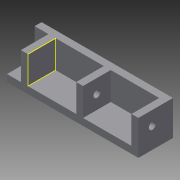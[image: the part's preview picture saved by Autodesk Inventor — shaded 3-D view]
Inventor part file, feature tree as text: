
AUTODESK INVENTOR PART (.ipt)
format: ipt  version: 2013 (Build 170138000, 138)  size: 116,736 bytes
history: native  units: in
note: dims shown in document units (in); Inventor stores cm internally (conversion verified against a paired STEP export)
features: sketch x5, extrude x4
ambient origin geometry x8: Origin, YZ Plane, XZ Plane, XY Plane, X Axis, Y Axis, Z Axis, Center Point
bodies: Solid1 (feature_tree)
feature tree (9):
  extrude  "Extrusion1"  Depth=4.75in
  extrude  "Extrusion2"  Depth=0.25in TaperAngle=0.0deg
  extrude  "Extrusion3"  Depth=1.0in TaperAngle=0.0deg
  sketch  "Sketch4"  dims[d8=0.5in d9=0.25in]
  extrude  "Extrusion4"  Depth=0.25in
  sketch  "Sketch1"  dims[d0=1.25in d1=4.75in]
  sketch  "Sketch2"  dims[d2=1.25in d3=0.25in d4=0.0in]
  sketch  "Sketch3"  dims[d5=0.25in d6=1.0in d7=0.0in]
  sketch  "Sketch5"  dims[d10=1.0in d11=1.75in d12=0.25in d13=1.0in d14=1.75in d15=1.0in d16=0.0in d17=0.5in d18=0.5in d19=0.25in d20=3.0in d21=0.0in]
